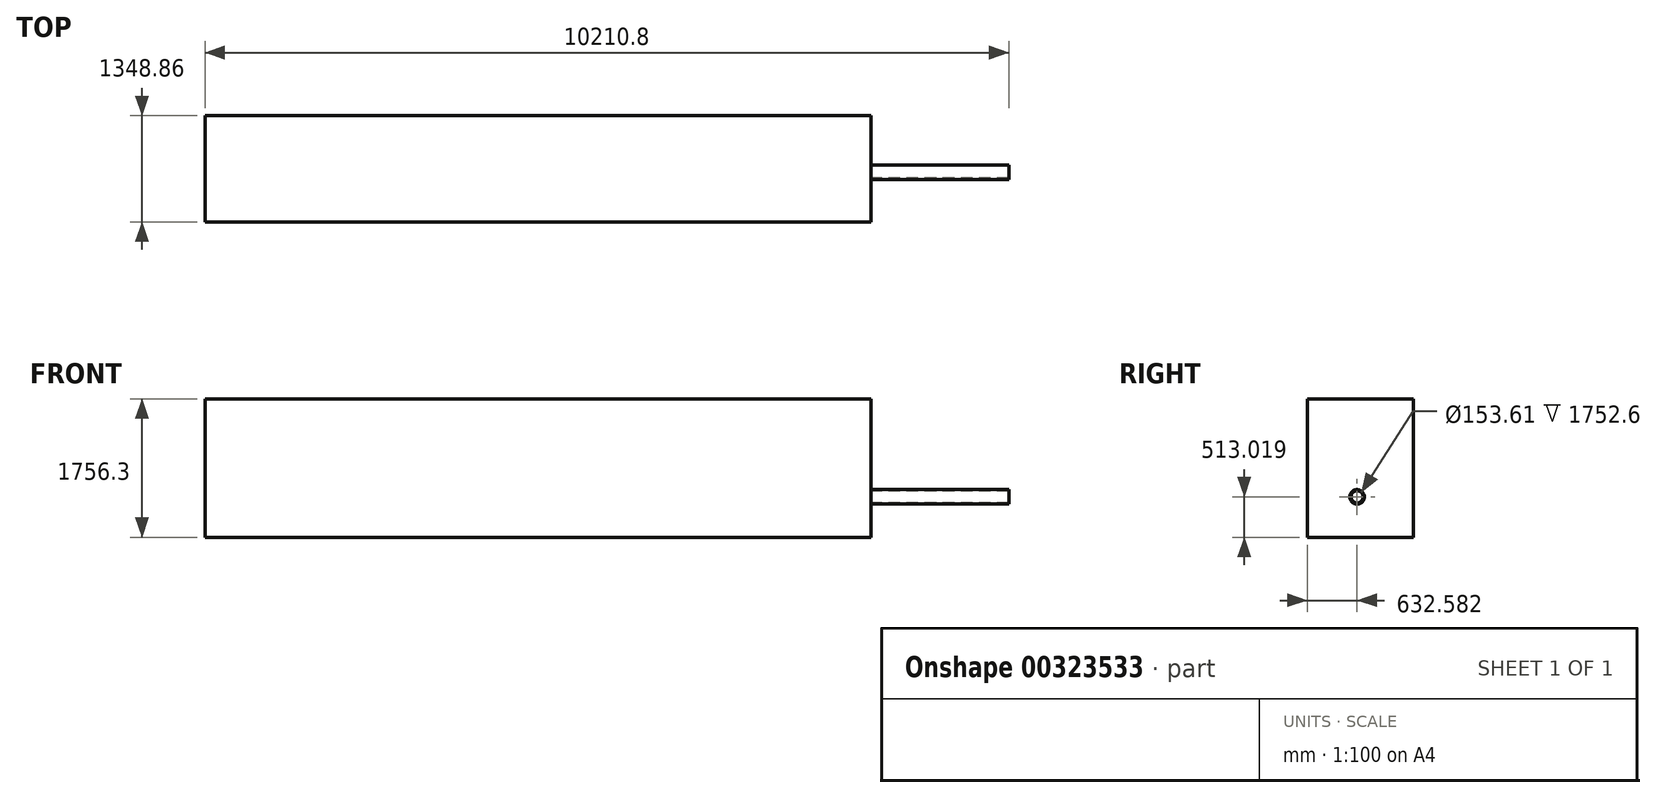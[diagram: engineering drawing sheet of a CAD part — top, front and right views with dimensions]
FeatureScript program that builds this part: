
annotation { "Feature Type Name" : "Feature", "Feature Type Description" : "" }
export const myFeature = defineFeature(function(context is Context, id is Id, definition is map)
    precondition{}
    {
        {
            var Q0;
            Q0=qCreatedBy(makeId("Right.planeOp"),FACE);
            var sketch = newSketch(context, id + "F0", { "sketchPlane" : qUnion([Q0])});
            skCircle(sketch, "E0", {"center": v(-103.6, 59) * mm, "radius": 92.07 * mm});
            skCircle(sketch, "E1", {"center": v(-103.6, 59) * mm, "radius": 76.8 * mm});
            skSolve(sketch);
        }
        {
            var Q0;
            Q0=makeQuery(id+"F0.imprint","IMPRINT",FACE,{"disambiguationData":[TD([[makeQuery(id+"F0.imprint","IMPRINT",EDGE,{"derivedFrom":sQuery(id+"F0.wireOp",EDGE,"E0")}),1.0]])]});
            extrude(context, id + "F1", {"entities" : qUnion([Q0]), "depth" : 1752.6 * mm});
        }
        {
            var Q0;
            Q0=qCreatedBy(makeId("Right.planeOp"),FACE);
            var sketch = newSketch(context, id + "F2", { "sketchPlane" : qUnion([Q0])});
            skLineSegment(sketch, "E2.bottom", {"start": v(-736.18, 1302.28) * mm, "end": v(612.68, 1302.28) * mm});
            skLineSegment(sketch, "E2.top", {"start": v(-736.18, -454.02) * mm, "end": v(612.68, -454.02) * mm});
            skLineSegment(sketch, "E2.left", {"start": v(-736.18, 1302.28) * mm, "end": v(-736.18, -454.02) * mm});
            skLineSegment(sketch, "E2.right", {"start": v(612.68, 1302.28) * mm, "end": v(612.68, -454.02) * mm});
            skSolve(sketch);
        }
        {
            var Q0;
            Q0 = qSketchRegion(id + "F2", true);
            extrude(context, id + "F3", {"entities" : qUnion([Q0]), "operationType" : NewBodyOperationType.ADD, "depth" : -8458.2 * mm});
        }
    });
